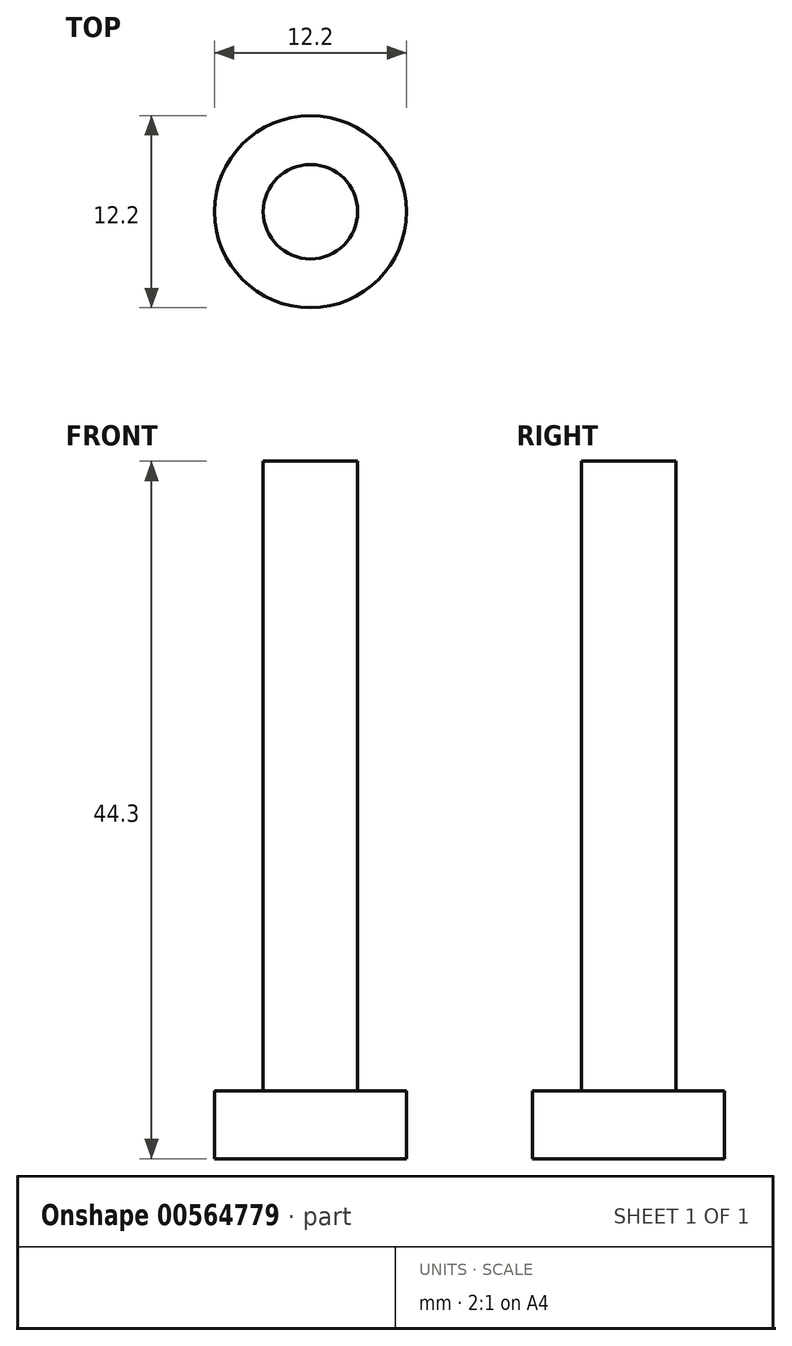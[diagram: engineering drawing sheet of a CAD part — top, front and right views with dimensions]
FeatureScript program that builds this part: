
annotation { "Feature Type Name" : "Feature", "Feature Type Description" : "" }
export const myFeature = defineFeature(function(context is Context, id is Id, definition is map)
    precondition{}
    {
        {
            var Q0;
            Q0=qCreatedBy(makeId("Top.planeOp"),FACE);
            var sketch = newSketch(context, id + "F0", { "sketchPlane" : qUnion([Q0])});
            skCircle(sketch, "E0", {"center": v(0, 0) * mm, "radius": 3 * mm});
            skSolve(sketch);
        }
        {
            var Q0;
            Q0=qSketchRegion(id+"F0",true);
            extrude(context, id + "F1", {"entities" : qUnion([Q0]), "depth" : 40 * mm, "offsetDistance" : 25 * mm});
        }
        {
            var Q0;
            Q0=makeQuery(id+"F1.opExtrude","CAP_FACE",FACE,{"disambiguationData":[OSD([sQuery(id+"F0.wireOp",EDGE,"E0")])],"isStart":true});
            var sketch = newSketch(context, id + "F2", { "sketchPlane" : qUnion([Q0])});
            skCircle(sketch, "E1", {"center": v(0, 0) * mm, "radius": 6.1 * mm});
            skSolve(sketch);
        }
        {
            var Q0;
            Q0=qSketchRegion(id+"F2",true);
            extrude(context, id + "F3", {"entities" : qUnion([Q0]), "operationType" : NewBodyOperationType.ADD, "depth" : 4.3 * mm, "offsetDistance" : 25 * mm});
        }
    });
